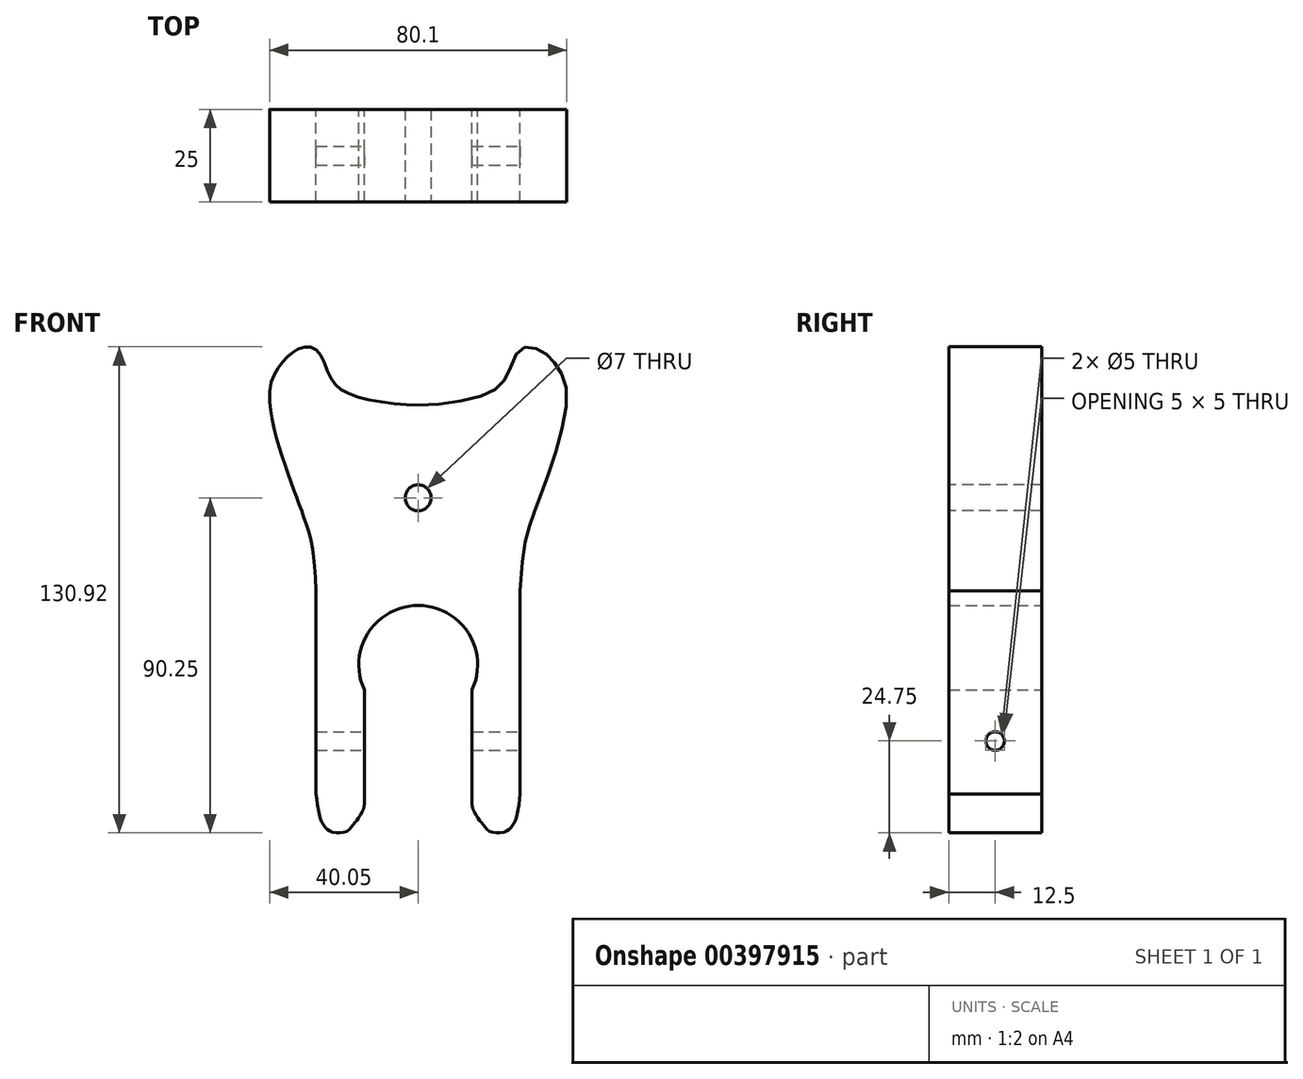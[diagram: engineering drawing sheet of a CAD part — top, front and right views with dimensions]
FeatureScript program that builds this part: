
annotation { "Feature Type Name" : "Feature", "Feature Type Description" : "" }
export const myFeature = defineFeature(function(context is Context, id is Id, definition is map)
    precondition{}
    {
        {
            var Q0;
            Q0=qCreatedBy(makeId("Front.planeOp"),FACE);
            var sketch = newSketch(context, id + "F0", { "sketchPlane" : qUnion([Q0])});
            skArc(sketch, "E0", {"start": v(14.5, -6.76) * mm, "mid": v(0, 16) * mm, "end": v(-14.5, -6.76) * mm});
            skLineSegment(sketch, "E1", {"start": v(0, 0) * mm, "end": v(0, 77.22) * mm, "construction": true});
            skLineSegment(sketch, "E2", {"start": v(-14.5, -37.2) * mm, "end": v(-14.5, -6.76) * mm});
            skLineSegment(sketch, "E3", {"start": v(-27.5, 20) * mm, "end": v(-27.5, -34.75) * mm});
            skLineSegment(sketch, "E4", {"start": v(-40, 73.7) * mm, "end": v(-40, 70.87) * mm});
            skFitSpline(sketch, "E5", {"points": [v(-27.5, 20) * mm, v(-30.34, 38.45) * mm, v(-35.58, 52.96) * mm, v(-40, 73.7) * mm, v(-36.78, 81.28) * mm, v(-32.47, 85) * mm, v(-27.5, 85) * mm, v(-23.87, 77.83) * mm, v(-17.95, 72.76) * mm, v(0, 70) * mm], "startDerivative": vector(-9.33, 219.79) * mm, "endDerivative": vector(119.38, -0.01) * mm});
            skFitSpline(sketch, "E6", {"points": [v(-27.5, -34.75) * mm, v(-26.5, -40.94) * mm, v(-25.01, -43.84) * mm, v(-23.17, -45) * mm, v(-19.68, -45) * mm, v(-17.84, -43.49) * mm, v(-16.46, -41.8) * mm, v(-14.5, -38.45) * mm], "startDerivative": vector(3.7, -33.92) * mm, "endDerivative": vector(20.52, 39.01) * mm});
            skArc(sketch, "E7.filletArc", {"start": v(-15.1, -39.58) * mm, "mid": v(-14.65, -38.43) * mm, "end": v(-14.5, -37.2) * mm});
            skArc(sketch, "E8.MirrorCS", {"start": v(15.1, -39.58) * mm, "mid": v(14.65, -38.43) * mm, "end": v(14.5, -37.2) * mm});
            skFitSpline(sketch, "E9.MirrorCS", {"points": [v(27.5, -34.75) * mm, v(26.5, -40.94) * mm, v(25.01, -43.84) * mm, v(23.17, -45) * mm, v(19.68, -45) * mm, v(17.84, -43.49) * mm, v(16.46, -41.8) * mm, v(14.5, -38.45) * mm], "startDerivative": vector(-3.7, -33.92) * mm, "endDerivative": vector(-20.52, 39.01) * mm});
            skFitSpline(sketch, "E10.MirrorCS", {"points": [v(27.5, 20) * mm, v(30.34, 38.45) * mm, v(35.58, 52.96) * mm, v(40, 73.7) * mm, v(36.78, 81.28) * mm, v(32.47, 85) * mm, v(27.5, 85) * mm, v(23.87, 77.83) * mm, v(17.95, 72.76) * mm, v(0, 70) * mm], "startDerivative": vector(9.33, 219.79) * mm, "endDerivative": vector(-119.38, -0.01) * mm});
            skLineSegment(sketch, "E11.MirrorCS", {"start": v(27.5, 20) * mm, "end": v(27.5, -34.75) * mm});
            skLineSegment(sketch, "E12.MirrorCS", {"start": v(14.5, -37.2) * mm, "end": v(14.5, -6.76) * mm});
            skSolve(sketch);
        }
        {
            var Q0;
            Q0 = qSketchRegion(id + "F0", true);
            extrude(context, id + "F1", {"entities" : qUnion([Q0]), "depth" : 25 * mm});
        }
        {
            var Q0;
            Q0=makeQuery(id+"F1.opExtrude","SWEPT_FACE",FACE,{"disambiguationData":[OSD([sQuery(id+"F0.wireOp",EDGE,"E11.MirrorCS")])]});
            var sketch = newSketch(context, id + "F2", { "sketchPlane" : qUnion([Q0])});
            skLineSegment(sketch, "E13", {"start": v(-12.5, -52.1) * mm, "end": v(-12.5, 7.9) * mm, "construction": true});
            skCircle(sketch, "E14", {"center": v(-12.5, -20.5) * mm, "radius": 2.5 * mm});
            skLineSegment(sketch, "E15", {"start": v(0, 0) * mm, "end": v(-63.59, 0) * mm, "construction": true});
            skSolve(sketch);
        }
        {
            var Q0;
            Q0 = qSketchRegion(id + "F2", true);
            extrude(context, id + "F3", {"entities" : qUnion([Q0]), "operationType" : NewBodyOperationType.REMOVE, "endBound" : BoundingType.SYMMETRIC, "oppositeDirection" : true, "depth" : 200 * mm});
        }
        {
            var Q0;
            Q0=makeQuery(id+"F1.opExtrude","CAP_FACE",FACE,{"disambiguationData":[OSD([sQuery(id+"F0.wireOp",EDGE,"E0"),sQuery(id+"F0.wireOp",EDGE,"E2"),sQuery(id+"F0.wireOp",EDGE,"E3"),sQuery(id+"F0.wireOp",EDGE,"E5"),sQuery(id+"F0.wireOp",EDGE,"E6"),sQuery(id+"F0.wireOp",EDGE,"E7.filletArc"),sQuery(id+"F0.wireOp",EDGE,"E8.MirrorCS"),sQuery(id+"F0.wireOp",EDGE,"E9.MirrorCS"),sQuery(id+"F0.wireOp",EDGE,"E10.MirrorCS"),sQuery(id+"F0.wireOp",EDGE,"E11.MirrorCS"),sQuery(id+"F0.wireOp",EDGE,"E12.MirrorCS")])],"isStart":false});
            var sketch = newSketch(context, id + "F4", { "sketchPlane" : qUnion([Q0])});
            skCircle(sketch, "E16", {"center": v(0, 45) * mm, "radius": 3.5 * mm});
            skSolve(sketch);
        }
        {
            var Q0;
            Q0 = qSketchRegion(id + "F4", true);
            extrude(context, id + "F5", {"entities" : qUnion([Q0]), "operationType" : NewBodyOperationType.REMOVE, "endBound" : BoundingType.THROUGH_ALL, "oppositeDirection" : true, "depth" : 25 * mm});
        }
    });
